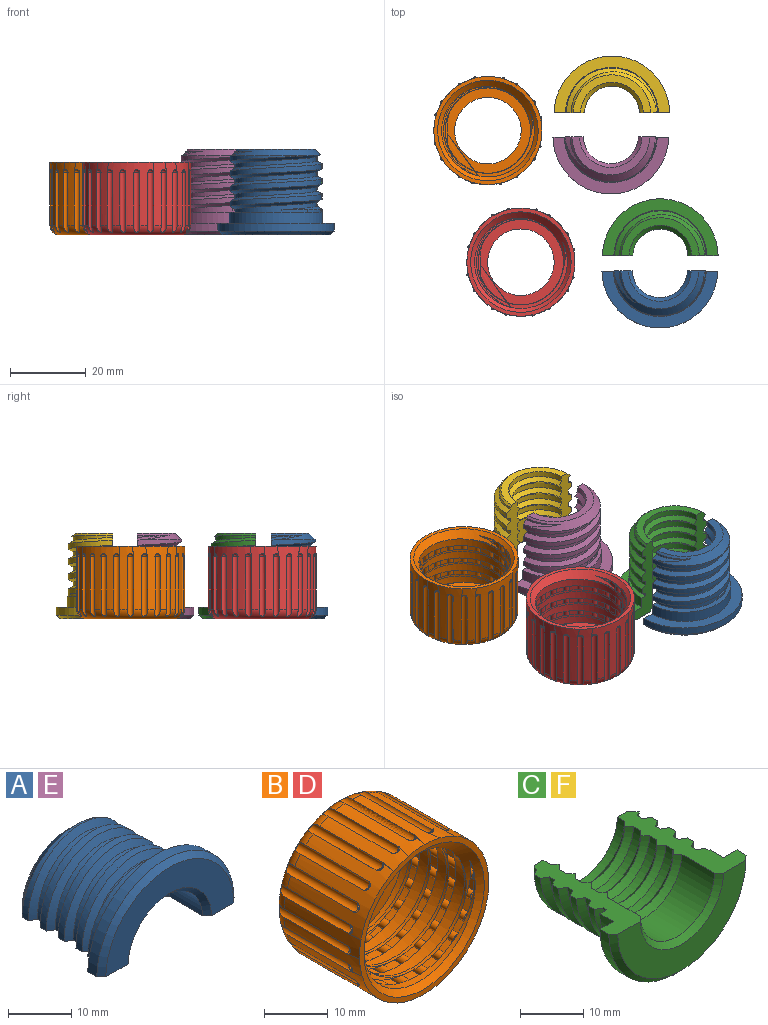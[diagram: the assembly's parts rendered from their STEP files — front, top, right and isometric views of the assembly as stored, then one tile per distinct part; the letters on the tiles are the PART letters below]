
ASSEMBLY  parts=6 mates=5
PART A: 44 faces, bbox 30.6x22.7x15.3 mm
  f0: extruded ~10.12x7.75mm, area 9.1mm2, adj f1,f2,f9,f38
  f1: bspline ~18.45x14.2mm, area 13.8mm2, adj f0,f9,f38,f43
  f2: plane 24.62x12.08mm, normal (0,1,0), area 41.8mm2, adj f0,f8,f9,f38,f42,f43
  f3: plane 30.6x15.05mm, normal (0,1,0), area 128.6mm2, adj f7,f8,f42,f43
  f4: cone r=8.3mm half-angle=45deg, axis (0,-1,0), area 38.4mm2, adj f6,f22,f42,f43
  f5: cone r=14.3mm half-angle=45deg, axis (0,1,0), area 65mm2, adj f6,f7,f42,f43
  f6: plane 28.6x14.05mm, normal (0,-1,0), area 182.9mm2, adj f4,f5,f42,f43
  f7: cylinder r=15.3mm len=30.6mm, axis (0,1,0), area 95.1mm2, adj f3,f5,f42,f43
  f8: cylinder r=12.3mm len=24.6mm, axis (0,1,0), area 114.4mm2, adj f2,f3,f42,f43
  f9: cylinder r=10.8mm len=21.59mm, axis (0,-1,0), area 40.1mm2, adj f0,f1,f2,f10,f42,f43
  f10: bspline ~24.6x14.2mm, area 53.3mm2, adj f9,f37,f42,f43
  f11: cone r=8.3mm half-angle=45deg, axis (0,1,0), area 33.9mm2, adj f12,f40,f42,f43
  f12: cone r=7.3mm half-angle=45deg, axis (0,-1,0), area 33.9mm2, adj f11,f13,f42,f43
  f13: cylinder r=8.3mm len=16.59mm, axis (0,1,0), area 40.9mm2, adj f12,f14,f42,f43
  f14: cone r=8.3mm half-angle=45deg, axis (0,1,0), area 33.9mm2, adj f13,f15,f42,f43
  f15: cone r=7.3mm half-angle=45deg, axis (0,-1,0), area 33.9mm2, adj f14,f16,f42,f43
  f16: cylinder r=8.3mm len=16.59mm, axis (0,1,0), area 40.9mm2, adj f15,f17,f42,f43
  f17: cone r=8.3mm half-angle=45deg, axis (0,1,0), area 33.9mm2, adj f16,f18,f42,f43
  f18: cone r=7.3mm half-angle=45deg, axis (0,-1,0), area 33.9mm2, adj f17,f19,f42,f43
  f19: cylinder r=8.3mm len=16.59mm, axis (0,1,0), area 40.9mm2, adj f18,f20,f42,f43
  f20: cone r=8.3mm half-angle=45deg, axis (0,1,0), area 33.9mm2, adj f19,f21,f42,f43
  f21: cone r=7.3mm half-angle=45deg, axis (0,-1,0), area 33.9mm2, adj f20,f22,f42,f43
  f22: cylinder r=8.3mm len=16.59mm, axis (0,1,0), area 185.9mm2, adj f4,f21,f42,f43
  f23: bspline ~24.6x14.2mm, area 53.3mm2, adj f24,f37,f42,f43
  f24: cylinder r=10.8mm len=21.59mm, axis (0,-1,0), area 37.9mm2, adj f23,f25,f42,f43
  f25: bspline ~24.6x14.2mm, area 53.3mm2, adj f24,f36,f42,f43
  f26: bspline ~24.6x14.2mm, area 53.3mm2, adj f27,f36,f42,f43
  f27: cylinder r=10.8mm len=21.59mm, axis (0,-1,0), area 37.9mm2, adj f26,f28,f42,f43
  f28: bspline ~24.6x14.2mm, area 53.3mm2, adj f27,f35,f42,f43
  f29: bspline ~10.65x6.9mm, area 8.3mm2, adj f30,f34,f39,f42
  f30: cylinder r=10.8mm len=8.44mm, axis (0,-1,0), area 2.9mm2, adj f29,f39,f42
  f31: bspline ~24.6x14.2mm, area 53.3mm2, adj f32,f35,f42,f43
  f32: cylinder r=10.8mm len=21.59mm, axis (0,-1,0), area 37.9mm2, adj f31,f33,f42,f43
  f33: bspline ~24.6x14.2mm, area 51.1mm2, adj f32,f34,f39,f42,f43
  f34: cylinder r=12.1mm len=19.52mm, axis (0,1,0), area 18.8mm2, adj f29,f33,f39,f42
  f35: cylinder r=12.1mm len=24.2mm, axis (0,1,0), area 51.2mm2, adj f28,f31,f42,f43
  f36: cylinder r=12.1mm len=24.2mm, axis (0,1,0), area 51.2mm2, adj f25,f26,f42,f43
  f37: cylinder r=12.1mm len=24.2mm, axis (0,1,0), area 51.2mm2, adj f10,f23,f42,f43
  f38: cylinder r=12.1mm len=2.68mm, axis (0,1,0), area 2mm2, adj f0,f1,f2,f43
  f39: cone r=10.3mm half-angle=45deg, axis (0,-1,0), area 75.4mm2, adj f29,f30,f33,f34,f41,f42,f43
  f40: cylinder r=8.3mm len=16.59mm, axis (0,1,0), area 40.9mm2, adj f11,f41,f42,f43
  f41: plane 20.59x10.05mm, normal (0,1,0), area 57.4mm2, adj f39,f40,f42,f43
  f42: plane 22.67x8mm, normal (0,0,-1), area 88.6mm2, adj f2,f3,f4,f5,f6,f7,f8,f9
  f43: plane 22.67x8mm, normal (0,0,-1), area 88.1mm2, adj f1,f2,f3,f4,f5,f6,f7,f8
PART B: 59 faces, bbox 31x19.2x31 mm
  f0: cylinder r=12.3mm len=24.6mm, axis (0,1,0), area 682.7mm2, adj f4,f6,f9
  f1: torus R=11.74mm, axis (0,1,0), area 269.2mm2, adj f2,f5,f12,f14,f16,f18,f20,f22
  f2: cylinder r=14.3mm len=28.6mm, axis (0,1,0), area 949.7mm2, adj f1,f3,f11,f12,f13,f14,f15,f16
  f3: plane 28.6x28.6mm, normal (0,-1,0), area 86.7mm2, adj f2,f9
  f4: plane 24x23.17mm, normal (0,-1,0), area 197.2mm2, adj f0,f6,f7,f8,f10
  f5: plane 23.48x23.48mm, normal (0,1,0), area 189.6mm2, adj f1,f10
  f6: bspline ~11.79x9.22mm, area 6.6mm2, adj f0,f4,f7
  f7: extruded ~8.97x1.42mm, area 3.1mm2, adj f4,f6,f8
  f8: cylinder r=11.3mm len=22.6mm, axis (0,-1,0), area 151.3mm2, adj f4,f7,f9
  f9: cone r=15.3mm half-angle=45deg, axis (0,-1,0), area 143.6mm2, adj f0,f3,f8
  f10: cylinder r=8.8mm len=17.6mm, axis (0,1,0), area 141.6mm2, adj f4,f5
  f11: sphere r=0.8mm, area 2mm2, adj f2,f12
  f12: cylinder r=0.8mm len=15.73mm, axis (0,-1,0), area 36.5mm2, adj f1,f2,f11
  f13: sphere r=0.8mm, area 2.3mm2, adj f2,f14
  f14: cylinder r=0.8mm len=15.73mm, axis (0,-1,0), area 37.8mm2, adj f1,f2,f13
  f15: sphere r=0.8mm, area 2.3mm2, adj f2,f16
  f16: cylinder r=0.8mm len=15.73mm, axis (0,-1,0), area 37.8mm2, adj f1,f2,f15
  f17: sphere r=0.8mm, area 2mm2, adj f2,f18
  f18: cylinder r=0.8mm len=15.73mm, axis (0,-1,0), area 37.8mm2, adj f1,f2,f17
  f19: sphere r=0.8mm, area 2.3mm2, adj f2,f20
  f20: cylinder r=0.8mm len=15.73mm, axis (0,-1,0), area 37.8mm2, adj f1,f2,f19
  f21: sphere r=0.8mm, area 2.3mm2, adj f2,f22
  f22: cylinder r=0.8mm len=15.73mm, axis (0,-1,0), area 37.8mm2, adj f1,f2,f21
  f23: sphere r=0.8mm, area 2mm2, adj f2,f24
  f24: cylinder r=0.8mm len=15.73mm, axis (0,-1,0), area 37.8mm2, adj f1,f2,f23
  f25: sphere r=0.8mm, area 2.3mm2, adj f2,f26
  f26: cylinder r=0.8mm len=15.73mm, axis (0,-1,0), area 37.8mm2, adj f1,f2,f25
  f27: sphere r=0.8mm, area 2.3mm2, adj f2,f28
  f28: cylinder r=0.8mm len=15.73mm, axis (0,-1,0), area 37.8mm2, adj f1,f2,f27
  f29: sphere r=0.8mm, area 2.3mm2, adj f2,f30
  f30: cylinder r=0.8mm len=15.73mm, axis (0,-1,0), area 37.8mm2, adj f1,f2,f29
  f31: sphere r=0.8mm, area 2mm2, adj f2,f32
  f32: cylinder r=0.8mm len=15.73mm, axis (0,-1,0), area 37.8mm2, adj f1,f2,f31
  f33: sphere r=0.8mm, area 2.3mm2, adj f2,f34
  f34: cylinder r=0.8mm len=15.73mm, axis (0,-1,0), area 37.8mm2, adj f1,f2,f33
  f35: sphere r=0.8mm, area 2.3mm2, adj f2,f36
  f36: cylinder r=0.8mm len=15.73mm, axis (0,-1,0), area 37.8mm2, adj f1,f2,f35
  f37: sphere r=0.8mm, area 2mm2, adj f2,f38
  f38: cylinder r=0.8mm len=15.73mm, axis (0,-1,0), area 37.8mm2, adj f1,f2,f37
  f39: sphere r=0.8mm, area 2.3mm2, adj f2,f40
  f40: cylinder r=0.8mm len=15.73mm, axis (0,-1,0), area 37.8mm2, adj f1,f2,f39
  f41: sphere r=0.8mm, area 2.3mm2, adj f2,f42
  f42: cylinder r=0.8mm len=15.73mm, axis (0,-1,0), area 37.8mm2, adj f1,f2,f41
  f43: sphere r=0.8mm, area 2mm2, adj f2,f44
  f44: cylinder r=0.8mm len=15.73mm, axis (0,-1,0), area 37.8mm2, adj f1,f2,f43
  f45: sphere r=0.8mm, area 2.3mm2, adj f2,f46
  f46: cylinder r=0.8mm len=15.73mm, axis (0,-1,0), area 37.8mm2, adj f1,f2,f45
  f47: sphere r=0.8mm, area 2.3mm2, adj f2,f48
  f48: cylinder r=0.8mm len=15.73mm, axis (0,-1,0), area 37.8mm2, adj f1,f2,f47
  f49: sphere r=0.8mm, area 2mm2, adj f2,f50
  f50: cylinder r=0.8mm len=15.73mm, axis (0,-1,0), area 37.8mm2, adj f1,f2,f49
  f51: sphere r=0.8mm, area 2.3mm2, adj f2,f52
  f52: cylinder r=0.8mm len=15.73mm, axis (0,-1,0), area 37.8mm2, adj f1,f2,f51
  f53: sphere r=0.8mm, area 2.3mm2, adj f2,f54
  f54: cylinder r=0.8mm len=15.73mm, axis (0,-1,0), area 37.8mm2, adj f1,f2,f53
  f55: sphere r=0.8mm, area 2mm2, adj f2,f56
  f56: cylinder r=0.8mm len=15.73mm, axis (0,-1,0), area 37.8mm2, adj f1,f2,f55
  f57: sphere r=0.8mm, area 2.3mm2, adj f2,f58
  f58: cylinder r=0.8mm len=15.73mm, axis (0,-1,0), area 37.8mm2, adj f1,f2,f57
PART C: 43 faces, bbox 30.6x23.6x15.3 mm
  f0: cylinder r=8.3mm len=16.59mm, axis (0,1,0), area 40.9mm2, adj f1,f18,f41,f42
  f1: plane 20.59x10.05mm, normal (0,1,0), area 57.4mm2, adj f0,f2,f41,f42
  f2: cone r=10.3mm half-angle=45deg, axis (0,-1,0), area 39.7mm2, adj f1,f19,f24,f41,f42
  f3: cylinder r=12.1mm len=24.2mm, axis (0,1,0), area 51.2mm2, adj f20,f29,f41,f42
  f4: cylinder r=12.1mm len=24.2mm, axis (0,1,0), area 51.2mm2, adj f21,f30,f41,f42
  f5: cylinder r=12.1mm len=24.2mm, axis (0,1,0), area 51.2mm2, adj f22,f31,f41,f42
  f6: cylinder r=12.1mm len=24.2mm, axis (0,1,0), area 52.6mm2, adj f23,f32,f34,f40,f41,f42
  f7: cylinder r=8.3mm len=16.59mm, axis (0,1,0), area 185.9mm2, adj f8,f38,f41,f42
  f8: cone r=7.3mm half-angle=45deg, axis (0,-1,0), area 33.9mm2, adj f7,f9,f41,f42
  f9: cone r=8.3mm half-angle=45deg, axis (0,1,0), area 33.9mm2, adj f8,f10,f41,f42
  f10: cylinder r=8.3mm len=16.59mm, axis (0,1,0), area 40.9mm2, adj f9,f11,f41,f42
  f11: cone r=7.3mm half-angle=45deg, axis (0,-1,0), area 33.9mm2, adj f10,f12,f41,f42
  f12: cone r=8.3mm half-angle=45deg, axis (0,1,0), area 33.9mm2, adj f11,f13,f41,f42
  f13: cylinder r=8.3mm len=16.59mm, axis (0,1,0), area 40.9mm2, adj f12,f14,f41,f42
  f14: cone r=7.3mm half-angle=45deg, axis (0,-1,0), area 33.9mm2, adj f13,f15,f41,f42
  f15: cone r=8.3mm half-angle=45deg, axis (0,1,0), area 33.9mm2, adj f14,f16,f41,f42
  f16: cylinder r=8.3mm len=16.59mm, axis (0,1,0), area 40.9mm2, adj f15,f17,f41,f42
  f17: cone r=7.3mm half-angle=45deg, axis (0,-1,0), area 33.9mm2, adj f16,f18,f41,f42
  f18: cone r=8.3mm half-angle=45deg, axis (0,1,0), area 33.9mm2, adj f0,f17,f41,f42
  f19: bspline ~24.6x14.2mm, area 13.6mm2, adj f2,f24,f42
  f20: bspline ~24.6x14.2mm, area 53.3mm2, adj f3,f25,f41,f42
  f21: bspline ~24.6x14.2mm, area 53.3mm2, adj f4,f26,f41,f42
  f22: bspline ~24.6x14.2mm, area 53.3mm2, adj f5,f27,f41,f42
  f23: bspline ~18.45x14.2mm, area 10.9mm2, adj f6,f28,f40,f41
  f24: cylinder r=10.8mm len=21.59mm, axis (0,-1,0), area 35.5mm2, adj f2,f19,f29,f41,f42
  f25: cylinder r=10.8mm len=21.59mm, axis (0,-1,0), area 37.9mm2, adj f20,f30,f41,f42
  f26: cylinder r=10.8mm len=21.59mm, axis (0,-1,0), area 37.9mm2, adj f21,f31,f41,f42
  f27: cylinder r=10.8mm len=21.59mm, axis (0,-1,0), area 37.9mm2, adj f22,f32,f41,f42
  f28: cylinder r=10.8mm len=0.69mm, axis (0,-1,0), area 0.3mm2, adj f23,f34,f40,f41
  f29: bspline ~24.6x14.2mm, area 53.3mm2, adj f3,f24,f41,f42
  f30: bspline ~24.6x14.2mm, area 53.3mm2, adj f4,f25,f41,f42
  f31: bspline ~24.6x14.2mm, area 53.3mm2, adj f5,f26,f41,f42
  f32: bspline ~24.6x14.2mm, area 53.3mm2, adj f6,f27,f41,f42
  f33: cylinder r=12.3mm len=24.6mm, axis (0,1,0), area 114.4mm2, adj f34,f37,f41,f42
  f34: plane 24.61x12.07mm, normal (0,1,0), area 17mm2, adj f6,f28,f33,f40,f41,f42
  f35: cylinder r=15.3mm len=30.6mm, axis (0,1,0), area 95.1mm2, adj f37,f39,f41,f42
  f36: plane 28.6x14.05mm, normal (0,-1,0), area 182.9mm2, adj f38,f39,f41,f42
  f37: plane 30.6x15.05mm, normal (0,1,0), area 128.6mm2, adj f33,f35,f41,f42
  f38: cone r=8.3mm half-angle=45deg, axis (0,-1,0), area 38.4mm2, adj f7,f36,f41,f42
  f39: cone r=14.3mm half-angle=45deg, axis (0,1,0), area 65mm2, adj f35,f36,f41,f42
  f40: extruded ~10.83x6.88mm, area 9.1mm2, adj f6,f23,f28,f34
  f41: plane 22.67x8mm, normal (0,0,1), area 88.6mm2, adj f0,f1,f2,f3,f4,f5,f6,f7
  f42: plane 22.67x8mm, normal (0,0,1), area 88.1mm2, adj f0,f1,f2,f3,f4,f5,f6,f7
PART D: same geometry as B
PART E: same geometry as A
PART F: same geometry as C
PLACE A rot(axis=(1,0,0),90deg) t=(-10.75,-40.03,8.46)mm
PLACE B rot(axis=(-1,0,0),90deg) t=(-56.23,-3.12,-11.65)mm
PLACE C rot(axis=(1,0,0),90deg) t=(-10.61,-36.47,8.46)mm
PLACE D rot(axis=(-1,0,0),90deg) t=(-47.51,-37.93,-11.65)mm fixed
PLACE E rot(axis=(1,0,0),90deg) t=(-23.72,-4.57,8.46)mm
PLACE F rot(axis=(1,0,0),90deg) t=(-23.41,1.33,8.46)mm
MATE planar F.f36 <-> B.f0  axis (0,0,-1) through (-23.41,9.06,-14.21)mm
MATE planar B.f0 <-> D.f0  axis (0,0,-1) through (-56.23,-3.12,-14.21)mm
MATE planar E.f6 <-> B.f0  axis (0,0,-1) through (-23.72,-12.3,-14.21)mm
MATE planar C.f36 <-> D.f0  axis (0,0,-1) through (-10.61,-28.74,-14.21)mm
MATE planar A.f6 <-> D.f0  axis (0,0,-1) through (-10.75,-47.75,-14.21)mm
